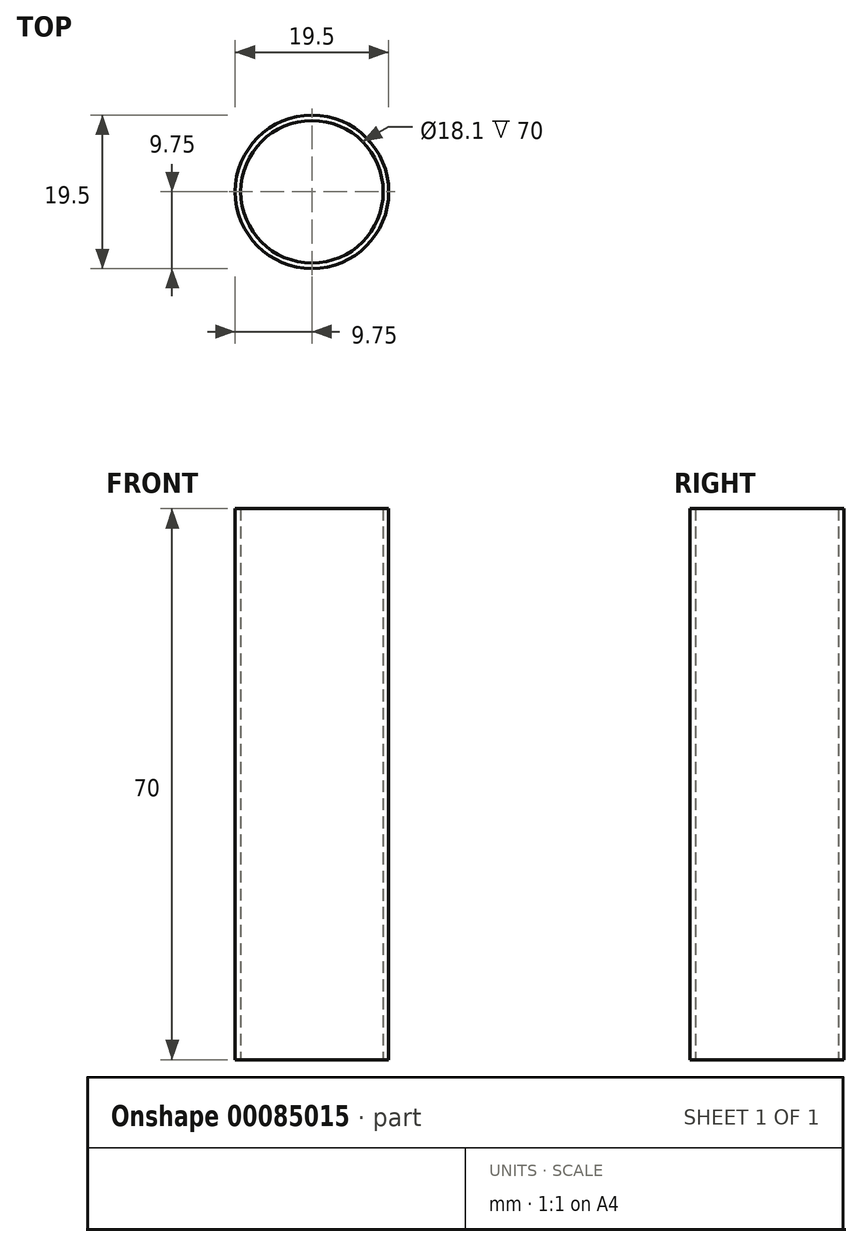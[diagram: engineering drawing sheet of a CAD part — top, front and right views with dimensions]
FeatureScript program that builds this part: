
annotation { "Feature Type Name" : "Feature", "Feature Type Description" : "" }
export const myFeature = defineFeature(function(context is Context, id is Id, definition is map)
    precondition{}
    {
        {
            var Q0;
            Q0=qCreatedBy(makeId("Top.planeOp"),FACE);
            var sketch = newSketch(context, id + "F0", { "sketchPlane" : qUnion([Q0])});
            skCircle(sketch, "E0", {"center": v(0, 0) * mm, "radius": 9.75 * mm});
            skCircle(sketch, "E1", {"center": v(0, 0) * mm, "radius": 9.05 * mm});
            skSolve(sketch);
        }
        {
            var Q0;
            Q0=makeQuery(id+"F0.imprint","IMPRINT",FACE,{"disambiguationData":[TD([[makeQuery(id+"F0.imprint","IMPRINT",EDGE,{"derivedFrom":sQuery(id+"F0.wireOp",EDGE,"E0")}),1.0]])]});
            extrude(context, id + "F1", {"entities" : qUnion([Q0]), "depth" : 70 * mm});
        }
    });
